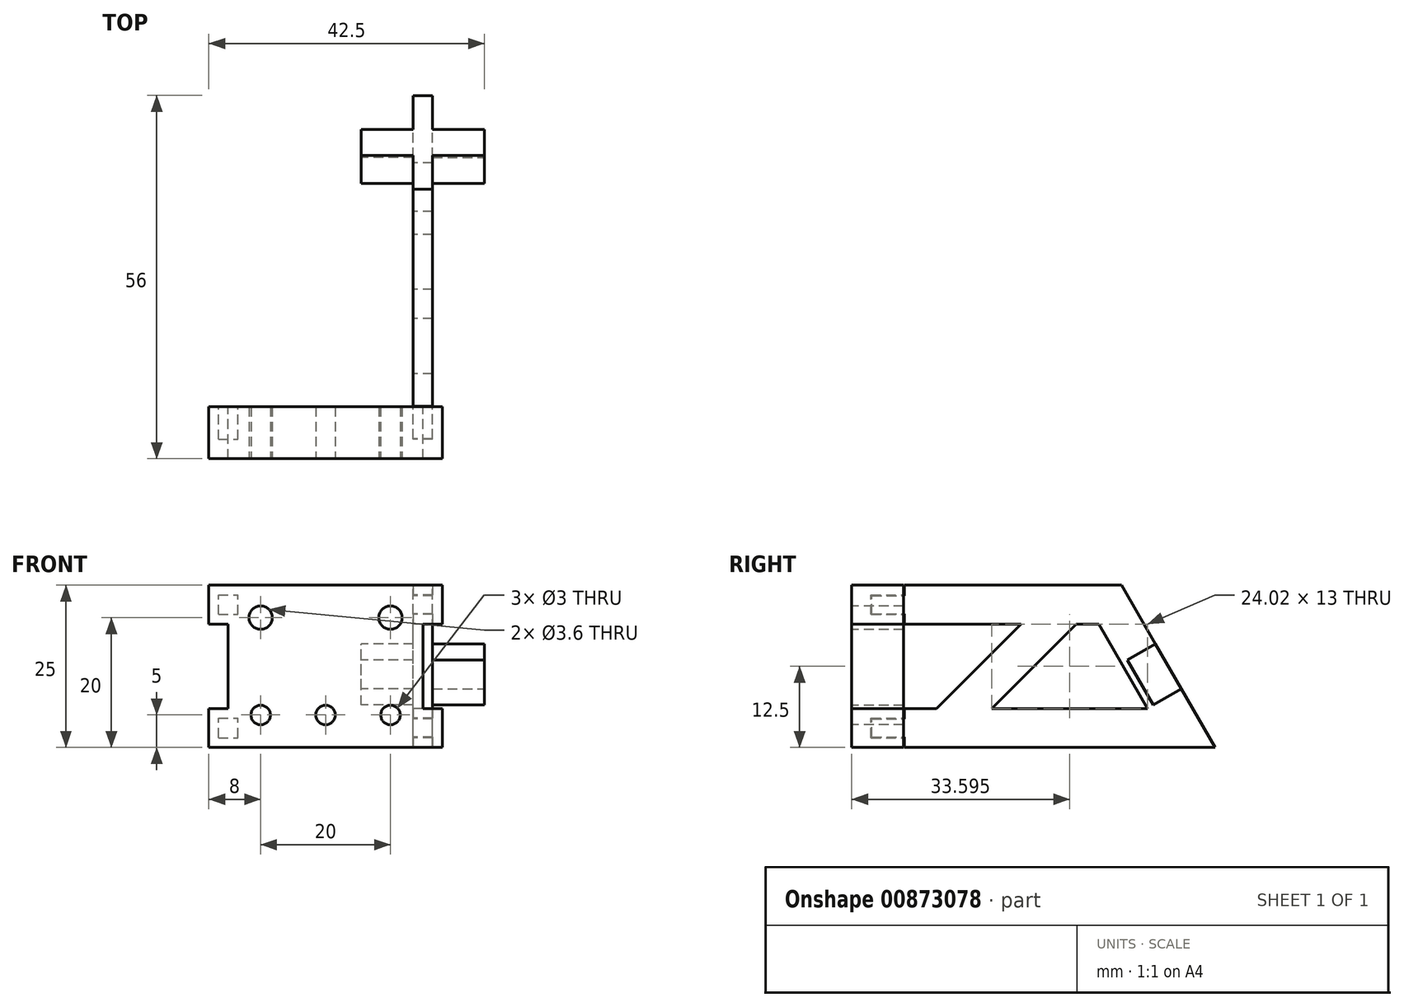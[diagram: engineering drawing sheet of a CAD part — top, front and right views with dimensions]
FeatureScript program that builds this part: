
annotation { "Feature Type Name" : "Feature", "Feature Type Description" : "" }
export const myFeature = defineFeature(function(context is Context, id is Id, definition is map)
    precondition{}
    {
        {
            var Q0;
            Q0=qCreatedBy(makeId("Front.planeOp"),FACE);
            var sketch = newSketch(context, id + "F0", { "sketchPlane" : qUnion([Q0])});
            skPoint(sketch, "E0.middle", {"position": v(0, 0) * mm});
            skCircle(sketch, "E1", {"center": v(-7.5, 5) * mm, "radius": 1.8 * mm});
            skCircle(sketch, "E2", {"center": v(12.5, 5) * mm, "radius": 1.8 * mm});
            skCircle(sketch, "E3", {"center": v(-7.5, -10) * mm, "radius": 1.5 * mm});
            skCircle(sketch, "E4", {"center": v(2.5, -10) * mm, "radius": 1.5 * mm});
            skCircle(sketch, "E5", {"center": v(12.5, -10) * mm, "radius": 1.5 * mm});
            skLineSegment(sketch, "E6", {"start": v(-12.5, -15) * mm, "end": v(17.5, -15) * mm});
            skLineSegment(sketch, "E7", {"start": v(-12.5, 10) * mm, "end": v(17.5, 10) * mm});
            skLineSegment(sketch, "E8", {"start": v(17.5, 10) * mm, "end": v(17.5, -15) * mm});
            skLineSegment(sketch, "E9", {"start": v(-12.5, 10) * mm, "end": v(-12.5, -15) * mm});
            skSolve(sketch);
        }
        {
            var Q0;
            Q0=makeQuery(id+"F0.imprint","IMPRINT",FACE,{"disambiguationData":[TD([[makeQuery(id+"F0.imprint","IMPRINT",EDGE,{"derivedFrom":sQuery(id+"F0.wireOp",EDGE,"E1")}),-1.0]])]});
            extrude(context, id + "F1", {"entities" : qUnion([Q0]), "oppositeDirection" : true, "depth" : 8 * mm, "offsetDistance" : 25 * mm});
        }
        {
            var Q0;
            Q0=makeQuery(id+"F1.opExtrude","CAP_FACE",FACE,{"disambiguationData":[OSD([sQuery(id+"F0.wireOp",EDGE,"E1"),sQuery(id+"F0.wireOp",EDGE,"E2"),sQuery(id+"F0.wireOp",EDGE,"E3"),sQuery(id+"F0.wireOp",EDGE,"E4"),sQuery(id+"F0.wireOp",EDGE,"E5"),sQuery(id+"F0.wireOp",EDGE,"E6"),sQuery(id+"F0.wireOp",EDGE,"E7"),sQuery(id+"F0.wireOp",EDGE,"E8"),sQuery(id+"F0.wireOp",EDGE,"E9")])],"isStart":false});
            var sketch = newSketch(context, id + "F2", { "sketchPlane" : qUnion([Q0])});
            skLineSegment(sketch, "E10.0", {"start": v(12.5, 10) * mm, "end": v(-17.5, 10) * mm});
            skLineSegment(sketch, "E10.2", {"start": v(12.5, -15) * mm, "end": v(-17.5, -15) * mm});
            skLineSegment(sketch, "E11", {"start": v(-17.5, 10) * mm, "end": v(-20.5, 10) * mm});
            skLineSegment(sketch, "E12", {"start": v(-20.5, 10) * mm, "end": v(-20.5, -15) * mm});
            skLineSegment(sketch, "E13", {"start": v(-20.5, -15) * mm, "end": v(-17.5, -15) * mm});
            skLineSegment(sketch, "E14", {"start": v(12.5, 10) * mm, "end": v(15.5, 10) * mm});
            skLineSegment(sketch, "E15", {"start": v(15.5, 10) * mm, "end": v(15.5, -15) * mm});
            skLineSegment(sketch, "E16", {"start": v(15.5, -15) * mm, "end": v(12.5, -15) * mm});
            skLineSegment(sketch, "E17.bottom", {"start": v(-19, 5.5) * mm, "end": v(-16, 5.5) * mm});
            skLineSegment(sketch, "E17.top", {"start": v(-19, 8.5) * mm, "end": v(-16, 8.5) * mm});
            skLineSegment(sketch, "E17.left", {"start": v(-19, 5.5) * mm, "end": v(-19, 8.5) * mm});
            skLineSegment(sketch, "E17.right", {"start": v(-16, 5.5) * mm, "end": v(-16, 8.5) * mm});
            skPoint(sketch, "E17.middle", {"position": v(-17.5, 7) * mm});
            skLineSegment(sketch, "E18.bottom", {"start": v(-19, -13.5) * mm, "end": v(-16, -13.5) * mm});
            skLineSegment(sketch, "E18.top", {"start": v(-19, -10.5) * mm, "end": v(-16, -10.5) * mm});
            skLineSegment(sketch, "E18.left", {"start": v(-19, -13.5) * mm, "end": v(-19, -10.5) * mm});
            skLineSegment(sketch, "E18.right", {"start": v(-16, -13.5) * mm, "end": v(-16, -10.5) * mm});
            skPoint(sketch, "E18.middle", {"position": v(-17.5, -12) * mm});
            skLineSegment(sketch, "E19", {"start": v(-2.5, 10) * mm, "end": v(-2.5, -15) * mm, "construction": true});
            skLineSegment(sketch, "E20.MirrorCS", {"start": v(11, 5.5) * mm, "end": v(11, 8.5) * mm});
            skLineSegment(sketch, "E21.MirrorCS", {"start": v(14, 8.5) * mm, "end": v(11, 8.5) * mm});
            skLineSegment(sketch, "E22.MirrorCS", {"start": v(14, 5.5) * mm, "end": v(14, 8.5) * mm});
            skLineSegment(sketch, "E23.MirrorCS", {"start": v(14, 5.5) * mm, "end": v(11, 5.5) * mm});
            skLineSegment(sketch, "E24.MirrorCS", {"start": v(14, -10.5) * mm, "end": v(11, -10.5) * mm});
            skLineSegment(sketch, "E25.MirrorCS", {"start": v(11, -13.5) * mm, "end": v(11, -10.5) * mm});
            skLineSegment(sketch, "E26.MirrorCS", {"start": v(14, -13.5) * mm, "end": v(11, -13.5) * mm});
            skLineSegment(sketch, "E27.MirrorCS", {"start": v(14, -13.5) * mm, "end": v(14, -10.5) * mm});
            skLineSegment(sketch, "E28", {"start": v(-20.5, 4) * mm, "end": v(-17.5, 4) * mm});
            skLineSegment(sketch, "E29", {"start": v(-20.5, -9) * mm, "end": v(-17.5, -9) * mm});
            skLineSegment(sketch, "E30", {"start": v(15.5, -9) * mm, "end": v(12.5, -9) * mm});
            skLineSegment(sketch, "E31", {"start": v(15.5, 4) * mm, "end": v(12.5, 4) * mm});
            skSolve(sketch);
        }
        {
            var Q0;
            {var subQ4=sQuery(id+"F2.wireOp",EDGE,"E13");Q0=makeQuery(id+"F2.imprint","IMPRINT",FACE,{"disambiguationData":[TD([[makeQuery(id+"F2.imprint","IMPRINT",EDGE,{"derivedFrom":subQ4}),1.0]])]});}
            var Q1;
            {var subQ5=sQuery(id+"F2.wireOp",EDGE,"E11");Q1=makeQuery(id+"F2.imprint","IMPRINT",FACE,{"disambiguationData":[TD([[makeQuery(id+"F2.imprint","IMPRINT",EDGE,{"derivedFrom":subQ5}),1.0]])]});}
            var Q2;
            {var subQ5=sQuery(id+"F2.wireOp",EDGE,"E14");Q2=makeQuery(id+"F2.imprint","IMPRINT",FACE,{"disambiguationData":[TD([[makeQuery(id+"F2.imprint","IMPRINT",EDGE,{"derivedFrom":subQ5}),-1.0]])]});}
            var Q3;
            {var subQ4=sQuery(id+"F2.wireOp",EDGE,"E16");Q3=makeQuery(id+"F2.imprint","IMPRINT",FACE,{"disambiguationData":[TD([[makeQuery(id+"F2.imprint","IMPRINT",EDGE,{"derivedFrom":subQ4}),-1.0]])]});}
            var Q4;
            {var subQ0=sQuery(id+"F2.wireOp",EDGE,"E17.left");Q4=makeQuery(id+"F2.imprint","IMPRINT",FACE,{"disambiguationData":[TD([[makeQuery(id+"F2.imprint","IMPRINT",EDGE,{"derivedFrom":subQ0}),-1.0]])]});}
            var Q5;
            {var subQ0=sQuery(id+"F2.wireOp",EDGE,"E18.left");Q5=makeQuery(id+"F2.imprint","IMPRINT",FACE,{"disambiguationData":[TD([[makeQuery(id+"F2.imprint","IMPRINT",EDGE,{"derivedFrom":subQ0}),-1.0]])]});}
            var Q6;
            {var subQ0=sQuery(id+"F2.wireOp",EDGE,"E27.MirrorCS");Q6=makeQuery(id+"F2.imprint","IMPRINT",FACE,{"disambiguationData":[TD([[makeQuery(id+"F2.imprint","IMPRINT",EDGE,{"derivedFrom":subQ0}),1.0]])]});}
            var Q7;
            {var subQ0=sQuery(id+"F2.wireOp",EDGE,"E22.MirrorCS");Q7=makeQuery(id+"F2.imprint","IMPRINT",FACE,{"disambiguationData":[TD([[makeQuery(id+"F2.imprint","IMPRINT",EDGE,{"derivedFrom":subQ0}),1.0]])]});}
            extrude(context, id + "F3", {"entities" : qUnion([Q0, Q1, Q2, Q3, Q4, Q5, Q6, Q7]), "operationType" : NewBodyOperationType.ADD, "oppositeDirection" : true, "depth" : 8 * mm, "offsetDistance" : 25 * mm});
        }
        {
            var Q0;
            {var subQ0=sQuery(id+"F2.wireOp",EDGE,"E17.right");Q0=makeQuery(id+"F2.imprint","IMPRINT",FACE,{"disambiguationData":[TD([[makeQuery(id+"F2.imprint","IMPRINT",EDGE,{"derivedFrom":subQ0}),1.0]])]});}
            var Q1;
            {var subQ0=sQuery(id+"F2.wireOp",EDGE,"E17.left");Q1=makeQuery(id+"F2.imprint","IMPRINT",FACE,{"disambiguationData":[TD([[makeQuery(id+"F2.imprint","IMPRINT",EDGE,{"derivedFrom":subQ0}),-1.0]])]});}
            var Q2;
            {var subQ0=sQuery(id+"F2.wireOp",EDGE,"E18.right");Q2=makeQuery(id+"F2.imprint","IMPRINT",FACE,{"disambiguationData":[TD([[makeQuery(id+"F2.imprint","IMPRINT",EDGE,{"derivedFrom":subQ0}),1.0]])]});}
            var Q3;
            {var subQ0=sQuery(id+"F2.wireOp",EDGE,"E18.left");Q3=makeQuery(id+"F2.imprint","IMPRINT",FACE,{"disambiguationData":[TD([[makeQuery(id+"F2.imprint","IMPRINT",EDGE,{"derivedFrom":subQ0}),-1.0]])]});}
            var Q4;
            {var subQ0=sQuery(id+"F2.wireOp",EDGE,"E27.MirrorCS");Q4=makeQuery(id+"F2.imprint","IMPRINT",FACE,{"disambiguationData":[TD([[makeQuery(id+"F2.imprint","IMPRINT",EDGE,{"derivedFrom":subQ0}),1.0]])]});}
            var Q5;
            {var subQ0=sQuery(id+"F2.wireOp",EDGE,"E25.MirrorCS");Q5=makeQuery(id+"F2.imprint","IMPRINT",FACE,{"disambiguationData":[TD([[makeQuery(id+"F2.imprint","IMPRINT",EDGE,{"derivedFrom":subQ0}),-1.0]])]});}
            var Q6;
            {var subQ0=sQuery(id+"F2.wireOp",EDGE,"E22.MirrorCS");Q6=makeQuery(id+"F2.imprint","IMPRINT",FACE,{"disambiguationData":[TD([[makeQuery(id+"F2.imprint","IMPRINT",EDGE,{"derivedFrom":subQ0}),1.0]])]});}
            var Q7;
            {var subQ0=sQuery(id+"F2.wireOp",EDGE,"E20.MirrorCS");Q7=makeQuery(id+"F2.imprint","IMPRINT",FACE,{"disambiguationData":[TD([[makeQuery(id+"F2.imprint","IMPRINT",EDGE,{"derivedFrom":subQ0}),-1.0]])]});}
            extrude(context, id + "F4", {"entities" : qUnion([Q0, Q1, Q2, Q3, Q4, Q5, Q6, Q7]), "operationType" : NewBodyOperationType.REMOVE, "oppositeDirection" : true, "depth" : 5 * mm, "offsetDistance" : 25 * mm});
        }
        {
            var Q0;
            Q0=makeQuery(id+"F4.boolean.opBoolean","COPY",FACE,{"derivedFrom":makeQuery(id+"F4.opExtrude","SWEPT_FACE",FACE,{"disambiguationData":[OSD([sQuery(id+"F2.wireOp",EDGE,"E17.right")])]})});
            var sketch = newSketch(context, id + "F5", { "sketchPlane" : qUnion([Q0])});
            skLineSegment(sketch, "E32.0", {"start": v(3, 8.5) * mm, "end": v(8, 8.5) * mm, "construction": true});
            skLineSegment(sketch, "E32.1", {"start": v(3, 5.5) * mm, "end": v(8, 5.5) * mm, "construction": true});
            skLineSegment(sketch, "E32.2", {"start": v(3, 5.5) * mm, "end": v(3, 8.5) * mm, "construction": true});
            skLineSegment(sketch, "E32.3", {"start": v(3, -10.5) * mm, "end": v(8, -10.5) * mm, "construction": true});
            skLineSegment(sketch, "E32.4", {"start": v(3, -13.5) * mm, "end": v(8, -13.5) * mm, "construction": true});
            skLineSegment(sketch, "E32.5", {"start": v(3, -13.5) * mm, "end": v(3, -10.5) * mm, "construction": true});
            skLineSegment(sketch, "E32.6", {"start": v(8, -9) * mm, "end": v(8, -10.6) * mm, "construction": true});
            skLineSegment(sketch, "E32.7", {"start": v(8, 10) * mm, "end": v(8, 8.5) * mm, "construction": true});
            skLineSegment(sketch, "E33.0", {"start": v(3.1, 8.4) * mm, "end": v(8, 8.4) * mm});
            skLineSegment(sketch, "E33.1", {"start": v(3.1, 5.6) * mm, "end": v(3.1, 8.4) * mm});
            skLineSegment(sketch, "E33.2", {"start": v(3.1, 5.6) * mm, "end": v(8, 5.6) * mm});
            skLineSegment(sketch, "E34.0", {"start": v(3.1, -10.6) * mm, "end": v(8, -10.6) * mm});
            skLineSegment(sketch, "E34.1", {"start": v(3.1, -13.4) * mm, "end": v(3.1, -10.6) * mm});
            skLineSegment(sketch, "E34.2", {"start": v(3.1, -13.4) * mm, "end": v(8, -13.4) * mm});
            skLineSegment(sketch, "E35.0", {"start": v(8.1, 10) * mm, "end": v(8.1, 8.4) * mm});
            skLineSegment(sketch, "E36", {"start": v(8, 8.4) * mm, "end": v(8.1, 8.4) * mm});
            skLineSegment(sketch, "E37", {"start": v(8, 5.6) * mm, "end": v(8.1, 5.6) * mm});
            skLineSegment(sketch, "E38.trimOffspring", {"start": v(8, 5.5) * mm, "end": v(8, 4) * mm, "construction": true});
            skLineSegment(sketch, "E39.0", {"start": v(8.1, -9) * mm, "end": v(8.1, -10.6) * mm});
            skLineSegment(sketch, "E40", {"start": v(8, -10.6) * mm, "end": v(8.1, -10.6) * mm});
            skLineSegment(sketch, "E41.trimOffspring", {"start": v(8, -13.5) * mm, "end": v(8, -15) * mm, "construction": true});
            skLineSegment(sketch, "E42.trimOffspring", {"start": v(8.1, -13.5) * mm, "end": v(8.1, -15) * mm});
            skLineSegment(sketch, "E43.trimOffspring", {"start": v(8.1, 5.6) * mm, "end": v(8.1, 4) * mm});
            skLineSegment(sketch, "E44", {"start": v(8.1, 10) * mm, "end": v(38.1, 10) * mm});
            skLineSegment(sketch, "E45", {"start": v(8.1, 4) * mm, "end": v(26.1, 4) * mm});
            skLineSegment(sketch, "E46", {"start": v(8.1, -15) * mm, "end": v(13.1, -15) * mm});
            skLineSegment(sketch, "E47", {"start": v(8.1, -9) * mm, "end": v(13.1, -9) * mm});
            skLineSegment(sketch, "E48", {"start": v(38.1, 4) * mm, "end": v(45.6, -9) * mm});
            skLineSegment(sketch, "E49", {"start": v(56, -15) * mm, "end": v(41.56, 10) * mm});
            skLineSegment(sketch, "E50", {"start": v(38.1, 10) * mm, "end": v(41.56, 10) * mm});
            skLineSegment(sketch, "E51", {"start": v(21.59, -9) * mm, "end": v(45.6, -9) * mm});
            skLineSegment(sketch, "E52", {"start": v(13.1, -15) * mm, "end": v(49.07, -15) * mm});
            skLineSegment(sketch, "E53", {"start": v(49.07, -15) * mm, "end": v(56, -15) * mm});
            skLineSegment(sketch, "E54", {"start": v(8, -13.4) * mm, "end": v(8.1, -13.4) * mm});
            skLineSegment(sketch, "E55", {"start": v(8.1, -13.4) * mm, "end": v(8.1, -13.5) * mm});
            skLineSegment(sketch, "E56", {"start": v(13.1, -9) * mm, "end": v(26.1, 4) * mm});
            skLineSegment(sketch, "E57", {"start": v(21.59, -9) * mm, "end": v(34.59, 4) * mm});
            skLineSegment(sketch, "E58.trimOffspring", {"start": v(34.59, 4) * mm, "end": v(38.1, 4) * mm});
            skSolve(sketch);
        }
        {
            var Q0;
            Q0=makeQuery(id+"F5.imprint","IMPRINT",FACE,{"disambiguationData":[TD([[makeQuery(id+"F5.imprint","IMPRINT",EDGE,{"derivedFrom":sQuery(id+"F5.wireOp",EDGE,"E34.0")}),-1.0]])]});
            var Q1;
            {var subQ0=sQuery(id+"F5.wireOp",EDGE,"E33.0");Q1=makeQuery(id+"F5.imprint","IMPRINT",FACE,{"disambiguationData":[TD([[makeQuery(id+"F5.imprint","IMPRINT",EDGE,{"derivedFrom":subQ0}),-1.0]])]});}
            extrude(context, id + "F6", {"entities" : qUnion([Q0, Q1]), "operationType" : NewBodyOperationType.ADD, "depth" : 3 * mm, "offsetDistance" : 25 * mm});
        }
        {
            var Q0;
            Q0=makeQuery(id+"F6.opExtrude","SWEPT_FACE",FACE,{"disambiguationData":[OSD([sQuery(id+"F5.wireOp",EDGE,"E49")])]});
            var sketch = newSketch(context, id + "F7", { "sketchPlane" : qUnion([Q0])});
            skLineSegment(sketch, "E59.0", {"start": v(-16, -40.99) * mm, "end": v(-16, -12.12) * mm});
            skLineSegment(sketch, "E59.1", {"start": v(-19, -40.99) * mm, "end": v(-19, -12.12) * mm});
            skLineSegment(sketch, "E60", {"start": v(-19, -26.56) * mm, "end": v(-16, -26.56) * mm, "construction": true});
            skLineSegment(sketch, "E61", {"start": v(-19, -22.56) * mm, "end": v(-27, -22.56) * mm});
            skLineSegment(sketch, "E62.MirrorCS", {"start": v(-19, -30.56) * mm, "end": v(-27, -30.56) * mm});
            skLineSegment(sketch, "E63", {"start": v(-27, -30.56) * mm, "end": v(-27, -22.56) * mm});
            skLineSegment(sketch, "E64", {"start": v(-17.5, -12.12) * mm, "end": v(-17.5, -40.99) * mm, "construction": true});
            skLineSegment(sketch, "E65.MirrorCS", {"start": v(-16, -22.56) * mm, "end": v(-8, -22.56) * mm});
            skLineSegment(sketch, "E66.MirrorCS", {"start": v(-8, -30.56) * mm, "end": v(-8, -22.56) * mm});
            skLineSegment(sketch, "E67.MirrorCS", {"start": v(-16, -30.56) * mm, "end": v(-8, -30.56) * mm});
            skSolve(sketch);
        }
        {
            var Q0;
            {var subQ0=sQuery(id+"F7.wireOp",EDGE,"E61");Q0=makeQuery(id+"F7.imprint","IMPRINT",FACE,{"disambiguationData":[TD([[makeQuery(id+"F7.imprint","IMPRINT",EDGE,{"derivedFrom":subQ0}),1.0]])]});}
            var Q1;
            {var subQ0=sQuery(id+"F7.wireOp",EDGE,"E65.MirrorCS");Q1=makeQuery(id+"F7.imprint","IMPRINT",FACE,{"disambiguationData":[TD([[makeQuery(id+"F7.imprint","IMPRINT",EDGE,{"derivedFrom":subQ0}),-1.0]])]});}
            extrude(context, id + "F8", {"entities" : qUnion([Q0, Q1]), "operationType" : NewBodyOperationType.ADD, "oppositeDirection" : true, "depth" : 5 * mm, "offsetDistance" : 25 * mm});
        }
    });
